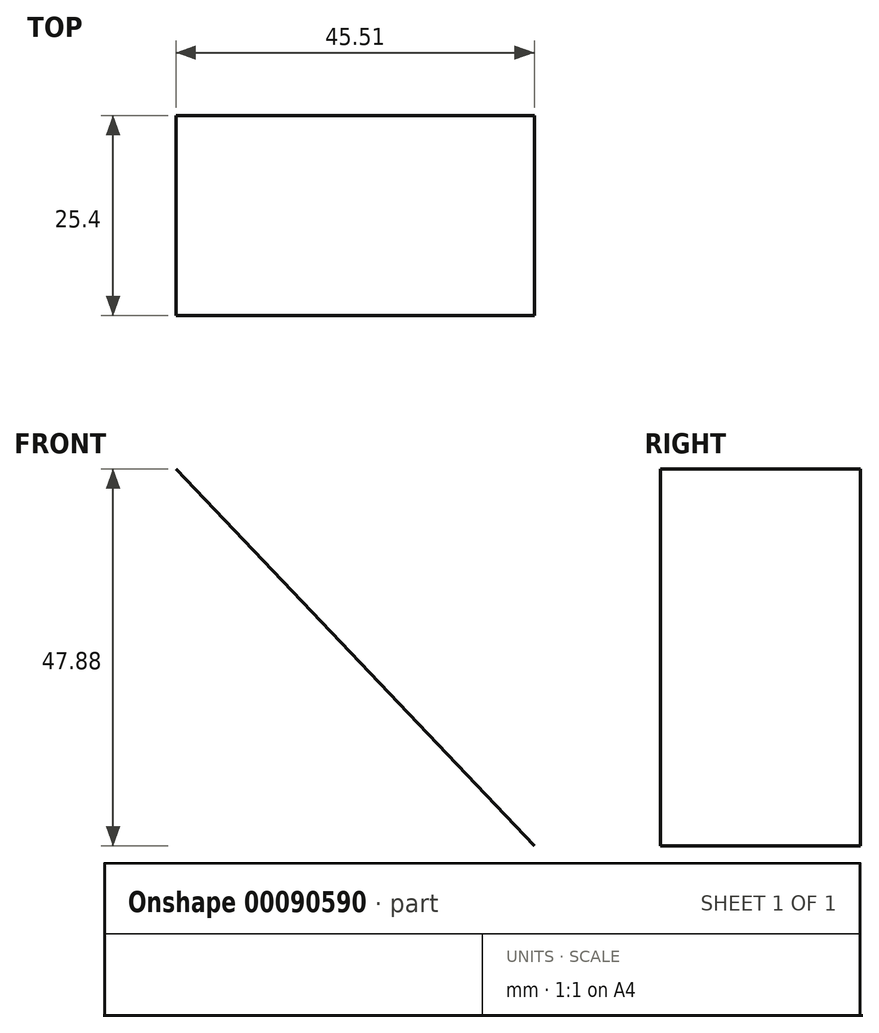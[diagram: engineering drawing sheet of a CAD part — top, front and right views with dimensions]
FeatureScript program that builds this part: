
annotation { "Feature Type Name" : "Feature", "Feature Type Description" : "" }
export const myFeature = defineFeature(function(context is Context, id is Id, definition is map)
    precondition{}
    {
        {
            var Q0;
            Q0=qCreatedBy(makeId("Front.planeOp"),FACE);
            var sketch = newSketch(context, id + "F0", { "sketchPlane" : qUnion([Q0])});
            skLineSegment(sketch, "E0", {"start": v(2.7, 45.11) * mm, "end": v(48.2, -2.77) * mm});
            skLineSegment(sketch, "E1", {"start": v(48.2, -2.77) * mm, "end": v(-9.78, -19.17) * mm});
            skLineSegment(sketch, "E2", {"start": v(-9.78, -19.17) * mm, "end": v(2.7, 45.11) * mm});
            skSolve(sketch);
        }
        {
            var Q0;
            Q0=sQuery(id+"F0.wireOp",EDGE,"E0");
            extrude(context, id + "F1", {"bodyType" : ToolBodyType.SURFACE, "surfaceEntities" : qUnion([Q0]), "depth" : 25.4 * mm});
        }
    });
